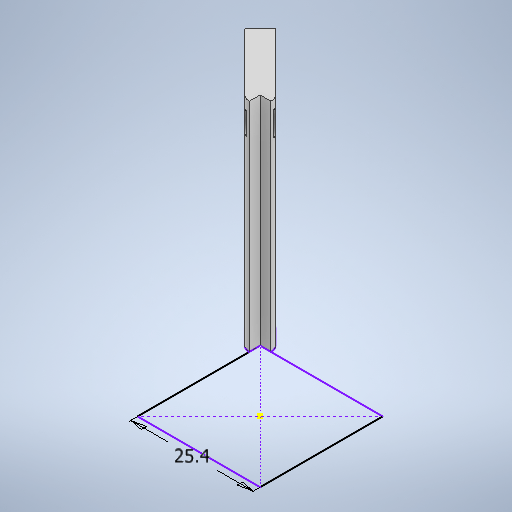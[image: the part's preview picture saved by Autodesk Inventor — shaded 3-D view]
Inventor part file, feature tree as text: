
AUTODESK INVENTOR PART (.ipt)
format: ipt  version: 2025.1 (Build 291241000, 241)  size: 306,176 bytes
history: native  units: in
note: dims shown in document units (in); Inventor stores cm internally (conversion verified against a paired STEP export)
features: extrude x3, sketch x3, projected_geometry x1
ambient origin geometry x8: Origin, YZ Plane, XZ Plane, XY Plane, X Axis, Y Axis, Z Axis, Center Point
bodies: Solid1 (feature_tree)
feature tree (7):
  extrude  "Extrusion1"  Depth=1.7717in TaperAngle=0.0deg
  extrude  "Extrusion2"  Depth=0.3543in TaperAngle=0.0deg
  extrude  "Extrusion3"  Depth=0.1772in
  sketch  "Sketch1"  dims[d0=1.0in d8=1.7717in d9=0.0in]
  sketch  "Sketch2"  dims[d10=0.3937in d11=0.3543in d12=0.0in]
  projected_geometry  "Projected Loop1"
  sketch  "Sketch3"  dims[d13=0.3543in d14=0.1772in d15=0.1772in d16=0.0197in d17=0.0197in d18=0.1969in d19=0.8543in d20=0.0in]
